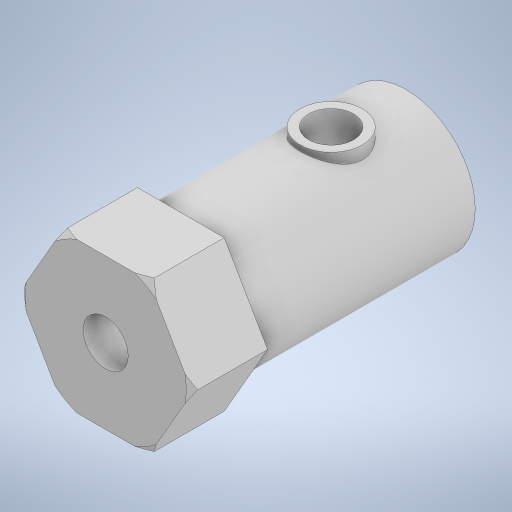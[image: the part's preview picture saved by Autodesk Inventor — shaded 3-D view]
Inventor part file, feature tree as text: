
AUTODESK INVENTOR PART (.ipt)
format: ipt  version: 2024 (Build 280153000, 153)  size: 667,648 bytes
history: native  units: mm
features: sketch x6, extrude x5, revolve x1, chamfer x1, plane x1
ambient origin geometry x8: Origin, YZ Plane, XZ Plane, XY Plane, X Axis, Y Axis, Z Axis, Center Point
bodies: Body1 (feature_tree)
feature tree (14):
  extrude  "Extrusion6"  Depth=6.0mm TaperAngle=0.0deg
  extrude  "Extrusion7"  Depth=5.15mm
  revolve  "Revolution1"  [1 undecoded]
  chamfer  "Chamfer3"  Distance=18.0mm
  extrude  "Extrusion8"  Depth=6.981317mm
  extrude  "Extrusion11"  Depth=0.125mm
  plane  "Work Plane2"
  extrude  "Extrusion12"  Depth=10.0mm TaperAngle=45.0deg
  sketch  "Sketch7"  dims[d24=12.0mm d25=6.0mm d26=0.0mm]
  sketch  "Sketch8"  dims[d27=11.0mm d28=5.15mm]
  sketch  "Sketch9"  dims[d29=4.5mm d30=1.573213mm d31=18.0mm d32=0.0mm]
  sketch  "Sketch10"  dims[d33=0.5mm d35=6.981317mm]
  sketch  "Sketch13"  dims[d38=90.0deg d39=0.125mm]
  sketch  "Sketch14"  dims[d40=0.104887mm d41=1.0mm d42=2.0mm d43=45.0deg d44=3.6mm d45=0.0mm d46=0.0mm d55=3.6mm d56=18.0mm d57=0.0mm d58=0.0mm d59=0.0mm d60=-4.0mm d61=5.0mm d62=18.0mm d63=10.0mm d64=0.0mm]
note: 1 required parameter value undecoded (feature->parameter linkage not recoverable at this tier; creation-order binding heuristic only, values carry confidence <= 0.55)
